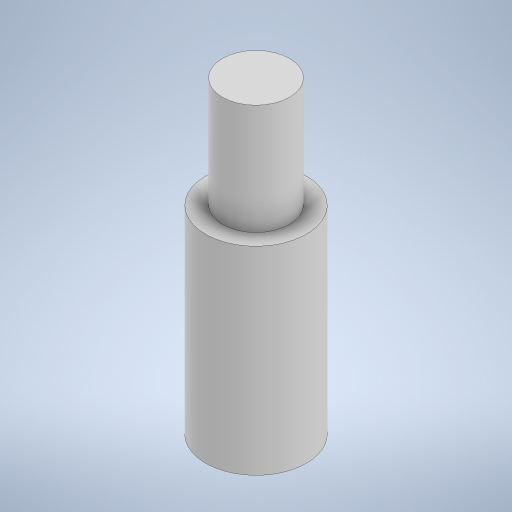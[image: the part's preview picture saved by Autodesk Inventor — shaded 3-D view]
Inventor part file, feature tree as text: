
AUTODESK INVENTOR PART (.ipt)
format: ipt  version: 2024 (Build 280153000, 153)  size: 239,104 bytes
history: native  units: in
note: dims shown in document units (in); Inventor stores cm internally (conversion verified against a paired STEP export)
features: extrude x3, sketch x3
ambient origin geometry x8: Origin, YZ Plane, XZ Plane, XY Plane, X Axis, Y Axis, Z Axis, Center Point
bodies: Solid1 (feature_tree)
feature tree (6):
  extrude  "Extrusion1"  Depth=0.315in TaperAngle=0.0deg
  extrude  "Extrusion2"  Depth=0.0394in TaperAngle=0.0deg
  extrude  "Extrusion3"  Depth=0.1969in
  sketch  "Sketch1"  dims[d0=0.18in d1=0.315in d2=0.0in]
  sketch  "Sketch2"  dims[d3=0.135in d4=0.0394in d5=0.0in]
  sketch  "Sketch3"  dims[d6=0.18in d7=0.12in d8=0.1969in d9=0.0in]
